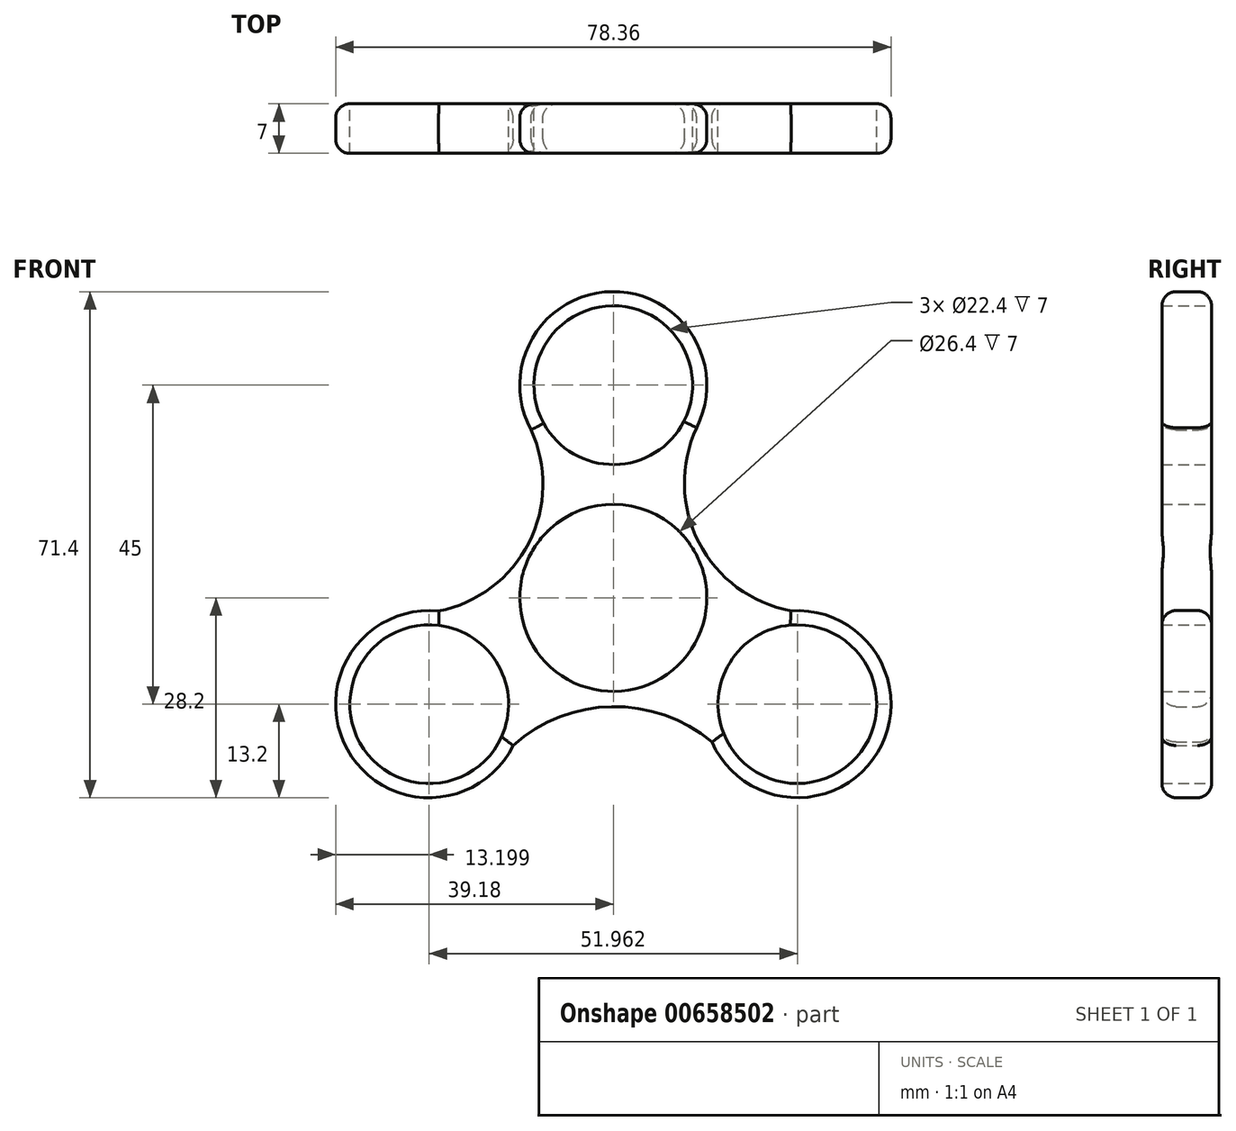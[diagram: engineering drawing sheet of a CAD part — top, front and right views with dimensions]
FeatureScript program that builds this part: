
annotation { "Feature Type Name" : "Feature", "Feature Type Description" : "" }
export const myFeature = defineFeature(function(context is Context, id is Id, definition is map)
    precondition{}
    {
        {
            var Q0;
            Q0=qCreatedBy(makeId("Front.planeOp"),FACE);
            var sketch = newSketch(context, id + "F0", { "sketchPlane" : qUnion([Q0])});
            skCircle(sketch, "E0", {"center": v(0, 0) * mm, "radius": 11.2 * mm});
            skCircle(sketch, "E1", {"center": v(0, 0) * mm, "radius": 13.2 * mm});
            skLineSegment(sketch, "E2", {"start": v(0, 0) * mm, "end": v(0, 13.2) * mm});
            skLineSegment(sketch, "E3", {"start": v(0, 0) * mm, "end": v(0, 30) * mm});
            skCircle(sketch, "E4", {"center": v(0, 30) * mm, "radius": 11.2 * mm});
            skCircle(sketch, "E5", {"center": v(0, 30) * mm, "radius": 13.2 * mm});
            skLineSegment(sketch, "E6", {"start": v(0, 0) * mm, "end": v(-25.98, -15) * mm});
            skCircle(sketch, "E7", {"center": v(-25.98, -15) * mm, "radius": 11.2 * mm});
            skCircle(sketch, "E8", {"center": v(-25.98, -15) * mm, "radius": 13.2 * mm});
            skLineSegment(sketch, "E9", {"start": v(0, 0) * mm, "end": v(25.98, -15) * mm});
            skCircle(sketch, "E10", {"center": v(25.98, -15) * mm, "radius": 11.2 * mm});
            skCircle(sketch, "E11", {"center": v(25.98, -15) * mm, "radius": 13.2 * mm});
            skArc(sketch, "E12", {"start": v(11.75, 24) * mm, "mid": v(12.07, 7.8) * mm, "end": v(25.08, -1.83) * mm});
            skArc(sketch, "E13", {"start": v(-24.65, -1.87) * mm, "mid": v(-11.7, 8.21) * mm, "end": v(-12.05, 24.62) * mm});
            skArc(sketch, "E14", {"start": v(13.91, -20.35) * mm, "mid": v(-0.2, -15.35) * mm, "end": v(-14.13, -20.82) * mm});
            skSolve(sketch);
        }
        {
            var Q0;
            Q0 = qSketchRegion(id + "F0", true);
            extrude(context, id + "F1", {"entities" : qUnion([Q0]), "depth" : 7 * mm, "offsetDistance" : 25.4 * mm});
        }
        {
            var Q0;
            Q0=makeQuery(id+"F1.opExtrude","CAP_EDGE",EDGE,{"disambiguationData":[OSD([sQuery(id+"F0.wireOp",EDGE,"E12")])],"isStart":false});
            var Q1;
            Q1=makeQuery(id+"F1.opExtrude","CAP_EDGE",EDGE,{"disambiguationData":[OSD([sQuery(id+"F0.wireOp",EDGE,"E5")])],"isStart":false});
            var Q2;
            Q2=makeQuery(id+"F1.opExtrude","CAP_EDGE",EDGE,{"disambiguationData":[OSD([sQuery(id+"F0.wireOp",EDGE,"E13")])],"isStart":false});
            var Q3;
            Q3=makeQuery(id+"F1.opExtrude","CAP_EDGE",EDGE,{"disambiguationData":[OSD([sQuery(id+"F0.wireOp",EDGE,"E8")])],"isStart":false});
            var Q4;
            Q4=makeQuery(id+"F1.opExtrude","CAP_EDGE",EDGE,{"disambiguationData":[OSD([sQuery(id+"F0.wireOp",EDGE,"E14")])],"isStart":false});
            var Q5;
            Q5=makeQuery(id+"F1.opExtrude","CAP_EDGE",EDGE,{"disambiguationData":[OSD([sQuery(id+"F0.wireOp",EDGE,"E11")])],"isStart":false});
            fillet(context, id + "F2", {"entities" : qUnion([Q0, Q1, Q2, Q3, Q4, Q5]), "radius" : 2 * mm, "tangentPropagation" : true, "allowEdgeOverflow" : false});
        }
        {
            var Q0;
            Q0=makeQuery(id+"F1.opExtrude","CAP_EDGE",EDGE,{"disambiguationData":[OSD([sQuery(id+"F0.wireOp",EDGE,"E5")])],"isStart":true});
            var Q1;
            Q1=makeQuery(id+"F1.opExtrude","CAP_EDGE",EDGE,{"disambiguationData":[OSD([sQuery(id+"F0.wireOp",EDGE,"E12")])],"isStart":true});
            var Q2;
            Q2=makeQuery(id+"F1.opExtrude","CAP_EDGE",EDGE,{"disambiguationData":[OSD([sQuery(id+"F0.wireOp",EDGE,"E14")])],"isStart":true});
            var Q3;
            Q3=makeQuery(id+"F1.opExtrude","CAP_EDGE",EDGE,{"disambiguationData":[OSD([sQuery(id+"F0.wireOp",EDGE,"E11")])],"isStart":true});
            var Q4;
            Q4=makeQuery(id+"F1.opExtrude","CAP_EDGE",EDGE,{"disambiguationData":[OSD([sQuery(id+"F0.wireOp",EDGE,"E13")])],"isStart":true});
            var Q5;
            Q5=makeQuery(id+"F1.opExtrude","CAP_EDGE",EDGE,{"disambiguationData":[OSD([sQuery(id+"F0.wireOp",EDGE,"E8")])],"isStart":true});
            fillet(context, id + "F3", {"entities" : qUnion([Q0, Q1, Q2, Q3, Q4, Q5]), "radius" : 2 * mm, "tangentPropagation" : true, "allowEdgeOverflow" : false});
        }
    });
